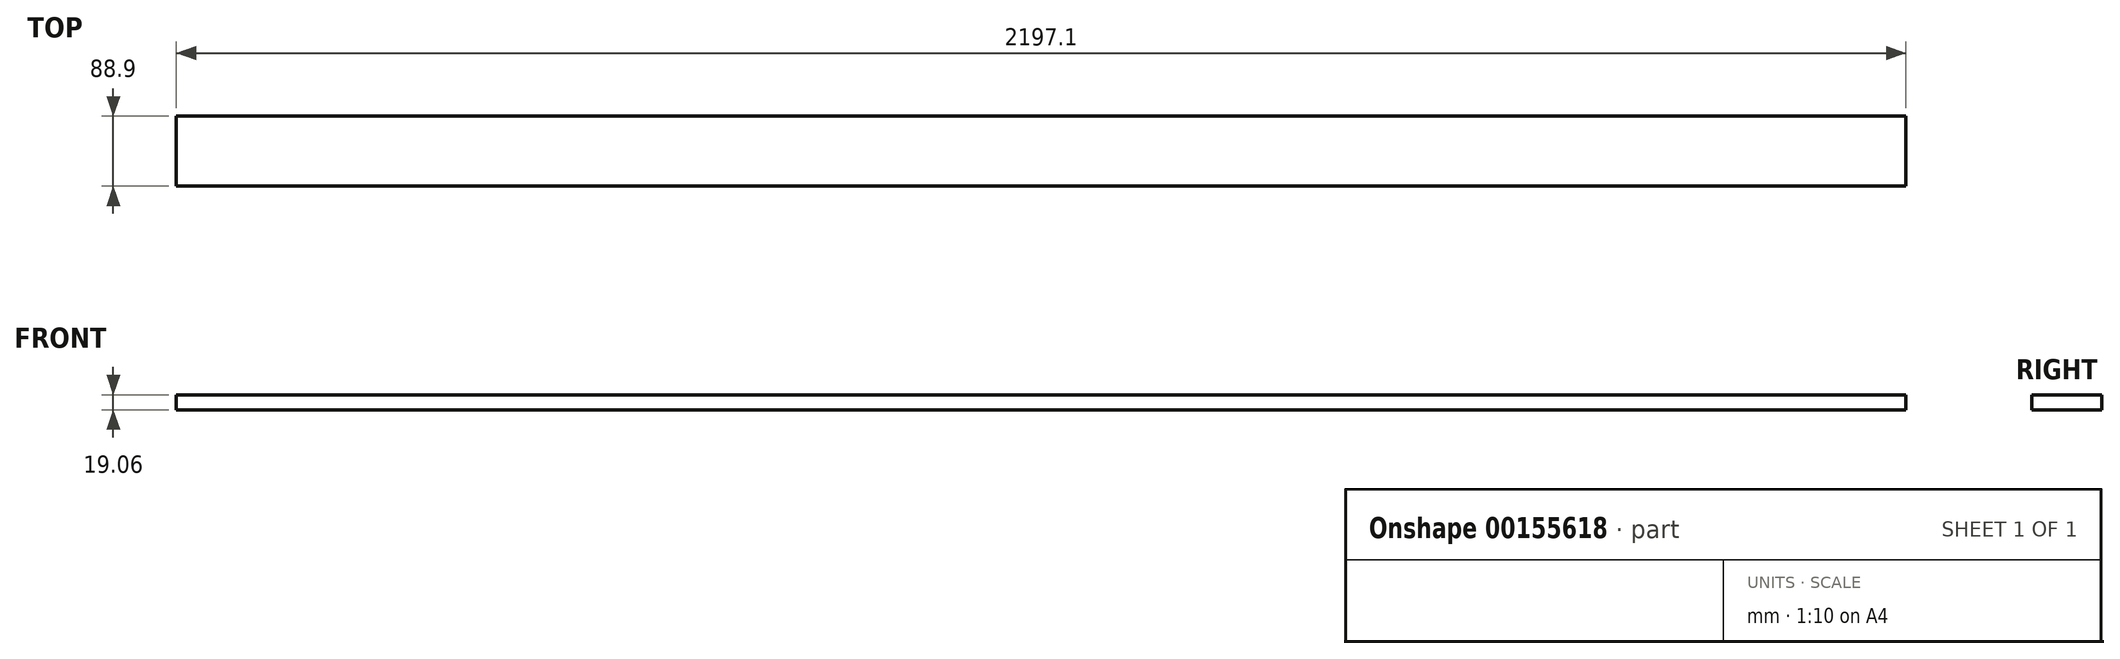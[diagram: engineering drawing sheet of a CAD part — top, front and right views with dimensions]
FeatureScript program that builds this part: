
annotation { "Feature Type Name" : "Feature", "Feature Type Description" : "" }
export const myFeature = defineFeature(function(context is Context, id is Id, definition is map)
    precondition{}
    {
        {
            var Q0;
            Q0=qCreatedBy(makeId("Right.planeOp"),FACE);
            var sketch = newSketch(context, id + "F0", { "sketchPlane" : qUnion([Q0])});
            skLineSegment(sketch, "E0.bottom", {"start": v(-44.45, 9.53) * mm, "end": v(44.45, 9.53) * mm});
            skLineSegment(sketch, "E0.top", {"start": v(-44.45, -9.52) * mm, "end": v(44.45, -9.52) * mm});
            skLineSegment(sketch, "E0.left", {"start": v(-44.45, 9.53) * mm, "end": v(-44.45, -9.52) * mm});
            skLineSegment(sketch, "E0.right", {"start": v(44.45, 9.53) * mm, "end": v(44.45, -9.52) * mm});
            skPoint(sketch, "E0.middle", {"position": v(0, 0) * mm});
            skSolve(sketch);
        }
        {
            var Q0;
            Q0=makeQuery(id+"F0.imprint","IMPRINT",FACE,{"disambiguationData":[TD([[makeQuery(id+"F0.imprint","IMPRINT",EDGE,{"derivedFrom":sQuery(id+"F0.wireOp",EDGE,"E0.bottom")}),-1.0]])]});
            extrude(context, id + "F1", {"entities" : qUnion([Q0]), "depth" : 2197.1 * mm});
        }
    });
